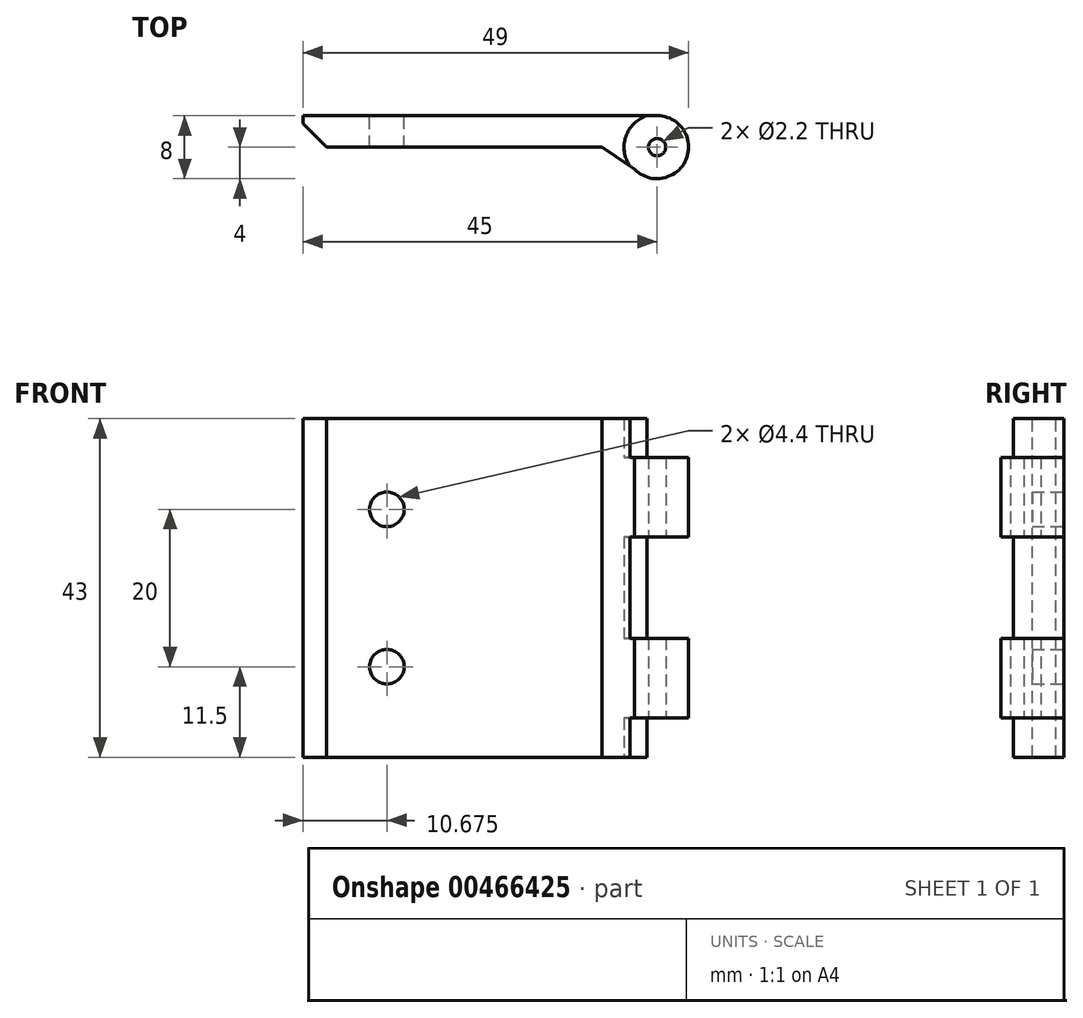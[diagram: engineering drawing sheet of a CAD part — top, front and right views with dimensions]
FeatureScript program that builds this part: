
annotation { "Feature Type Name" : "Feature", "Feature Type Description" : "" }
export const myFeature = defineFeature(function(context is Context, id is Id, definition is map)
    precondition{}
    {
        {
            var Q0;
            Q0=qCreatedBy(makeId("Top.planeOp"),FACE);
            var sketch = newSketch(context, id + "F0", { "sketchPlane" : qUnion([Q0])});
            skLineSegment(sketch, "E0.bottom", {"start": v(22.5, -2) * mm, "end": v(-22.5, -2) * mm});
            skLineSegment(sketch, "E0.top", {"start": v(22.5, 2) * mm, "end": v(-22.5, 2) * mm});
            skLineSegment(sketch, "E0.left", {"start": v(22.5, -2) * mm, "end": v(22.5, 2) * mm});
            skLineSegment(sketch, "E0.right", {"start": v(-22.5, -2) * mm, "end": v(-22.5, 2) * mm});
            skPoint(sketch, "E0.middle", {"position": v(0, 0) * mm});
            skCircle(sketch, "E1", {"center": v(22.5, -2) * mm, "radius": 4 * mm});
            skCircle(sketch, "E2", {"center": v(22.5, -2) * mm, "radius": 1.1 * mm});
            skSolve(sketch);
        }
        {
            var Q0;
            {var subQ1=sQuery(id+"F0.wireOp",EDGE,"E0.top");Q0=makeQuery(id+"F0.imprint","IMPRINT",FACE,{"disambiguationData":[TD([[makeQuery(id+"F0.imprint","IMPRINT",EDGE,{"derivedFrom":subQ1}),1.0]])]});}
            var Q1;
            {var subQ0=sQuery(id+"F0.wireOp",EDGE,"E1");var subQ1=sQuery(id+"F0.wireOp",EDGE,"E0.bottom");var subQ2=makeQuery(id+"F0.imprint","INTERSECT",VERTEX,{"derivedFrom":[subQ1,subQ0]});Q1=makeQuery(id+"F0.imprint","IMPRINT",FACE,{"disambiguationData":[TD([[makeQuery(id+"F0.imprint","IMPRINT",EDGE,{"disambiguationData":[TD([[subQ2,1.0]])],"derivedFrom":subQ1}),-1.0]])]});}
            var Q2;
            {var subQ0=sQuery(id+"F0.wireOp",EDGE,"E1");var subQ1=sQuery(id+"F0.wireOp",EDGE,"E0.bottom");var subQ2=makeQuery(id+"F0.imprint","INTERSECT",VERTEX,{"derivedFrom":[subQ1,subQ0]});Q2=makeQuery(id+"F0.imprint","IMPRINT",FACE,{"disambiguationData":[TD([[makeQuery(id+"F0.imprint","IMPRINT",EDGE,{"disambiguationData":[TD([[subQ2,1.0]])],"derivedFrom":subQ1}),1.0]])]});}
            extrude(context, id + "F1", {"entities" : qUnion([Q0, Q1, Q2]), "depth" : 43 * mm, "offsetDistance" : 25 * mm});
        }
        {
            var Q0;
            Q0=makeQuery(id+"F1.opExtrude","SWEPT_EDGE",EDGE,{"disambiguationData":[OSD([sQuery(id+"F0.wireOp",EDGE,"E0.bottom"),sQuery(id+"F0.wireOp",EDGE,"E1")])]});
            var Q1;
            Q1=makeQuery(id+"F1.opExtrude","SWEPT_EDGE",EDGE,{"disambiguationData":[OSD([sQuery(id+"F0.wireOp",EDGE,"E0.bottom"),sQuery(id+"F0.wireOp",EDGE,"E0.right")])]});
            chamfer(context, id + "F2", {"entities" : qUnion([Q0, Q1]), "width" : 3 * mm, "tangentPropagation" : true});
        }
        {
            var Q0;
            Q0=makeQuery(id+"F1.opExtrude","SWEPT_FACE",FACE,{"disambiguationData":[OSD([sQuery(id+"F0.wireOp",EDGE,"E0.bottom")])]});
            var sketch = newSketch(context, id + "F3", { "sketchPlane" : qUnion([Q0])});
            skLineSegment(sketch, "E3", {"start": v(-11.82, 43) * mm, "end": v(-11.82, 0) * mm, "construction": true});
            skPoint(sketch, "E4", {"position": v(-11.82, 11.5) * mm});
            skPoint(sketch, "E5", {"position": v(-11.82, 31.5) * mm});
            skPoint(sketch, "E6", {"position": v(-11.82, 21.5) * mm});
            skLineSegment(sketch, "E7", {"start": v(16.18, 21.5) * mm, "end": v(-19.5, 21.5) * mm, "construction": true});
            skSolve(sketch);
        }
        {
            var Q0;
            Q0=sQuery(id+"F3.wireOp",VERTEX,"E5");
            var Q1;
            Q1=sQuery(id+"F3.wireOp",VERTEX,"E4");
            var Q2;
            Q2=makeQuery(id+"F1.opExtrude","SWEPT_BODY",BODY,{"disambiguationData":[OSD([sQuery(id+"F0.wireOp",EDGE,"E0.bottom"),sQuery(id+"F0.wireOp",EDGE,"E0.top"),sQuery(id+"F0.wireOp",EDGE,"E0.left"),sQuery(id+"F0.wireOp",EDGE,"E0.right"),sQuery(id+"F0.wireOp",EDGE,"E1"),sQuery(id+"F0.wireOp",EDGE,"E2")])]});
            hole(context, id + "F4", {"style" : HoleStyle.SIMPLE, "endStyle" : HoleEndStyle.THROUGH, "standardTappedOrClearance" : lookupTablePath({ "standard" : "ISO", "fit" : "Normal", "size" : "M4", "type" : "Clearance" }), "standardBlindInLast" : lookupTablePath({ "fit" : "Standard", "standard" : "ISO", "size" : "M4", "type" : "Clearance" }), "holeDiameter" : 4.4 * mm, "majorDiameter" : 5 * mm, "isTappedThrough" : true, "tappedDepth" : 12 * mm, "tapClearance" : 3, "locations" : qUnion([Q0, Q1]), "scope" : qUnion([Q2]), "startStyle" : HoleStartStyle.PART});
        }
        {
            var Q0;
            {var subQ0=sQuery(id+"F0.wireOp",EDGE,"E0.left");var subQ1=sQuery(id+"F0.wireOp",EDGE,"E0.bottom");var subQ2=makeQuery(id+"F0.imprint","INTERSECT",VERTEX,{"derivedFrom":[subQ1,subQ0]});Q0=makeQuery(id+"F0.imprint","IMPRINT",FACE,{"disambiguationData":[TD([[makeQuery(id+"F0.imprint","IMPRINT",EDGE,{"disambiguationData":[TD([[subQ2,-1.0]])],"derivedFrom":subQ1}),1.0]])]});}
            var sketch = newSketch(context, id + "F5", { "sketchPlane" : qUnion([Q0])});
            skCircle(sketch, "E8", {"center": v(22.5, -2) * mm, "radius": 4.2 * mm});
            skSolve(sketch);
        }
        {
            var Q0;
            Q0 = qSketchRegion(id + "F5", true);
            extrude(context, id + "F6", {"entities" : qUnion([Q0]), "operationType" : NewBodyOperationType.REMOVE, "depth" : 5 * mm, "offsetDistance" : 25 * mm});
        }
        {
            var Q0;
            Q0 = qSketchRegion(id + "F5", true);
            extrude(context, id + "F7", {"entities" : qUnion([Q0]), "operationType" : NewBodyOperationType.REMOVE, "depth" : 28 * mm, "offsetDistance" : 25 * mm, "hasSecondDirection" : true, "secondDirectionOppositeDirection" : true, "secondDirectionDepth" : -15.1 * mm});
        }
        {
            var Q0;
            Q0 = qSketchRegion(id + "F5", true);
            extrude(context, id + "F8", {"entities" : qUnion([Q0]), "operationType" : NewBodyOperationType.REMOVE, "depth" : 50 * mm, "offsetDistance" : 25 * mm, "hasSecondDirection" : true, "secondDirectionOppositeDirection" : true, "secondDirectionDepth" : -38.1 * mm});
        }
    });
